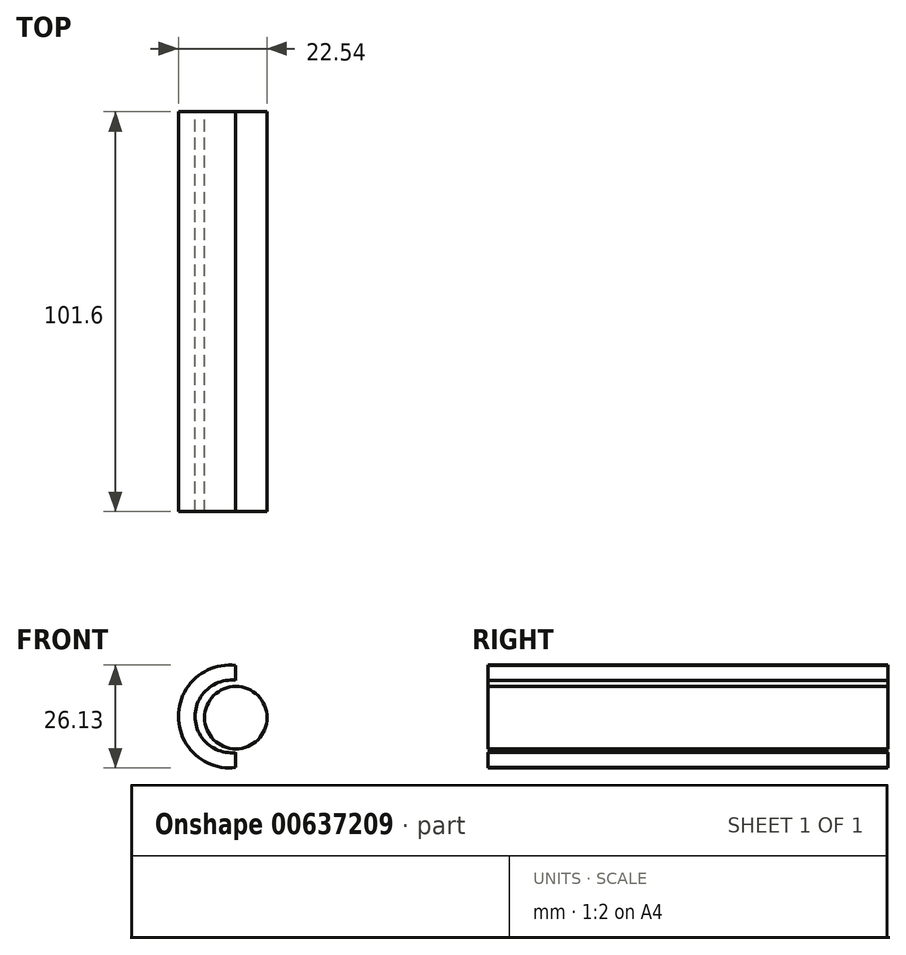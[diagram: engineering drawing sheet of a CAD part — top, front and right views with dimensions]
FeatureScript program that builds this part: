
annotation { "Feature Type Name" : "Feature", "Feature Type Description" : "" }
export const myFeature = defineFeature(function(context is Context, id is Id, definition is map)
    precondition{}
    {
        {
            var Q0;
            Q0=qCreatedBy(makeId("Front.planeOp"),FACE);
            var sketch = newSketch(context, id + "F0", { "sketchPlane" : qUnion([Q0])});
            skArc(sketch, "E0", {"start": v(0, 9.45) * mm, "mid": v(-10.35, 0.29) * mm, "end": v(0, -8.88) * mm});
            skLineSegment(sketch, "E1", {"start": v(0, 9.45) * mm, "end": v(0, 13.26) * mm});
            skLineSegment(sketch, "E2", {"start": v(0, -8.88) * mm, "end": v(0, -12.69) * mm});
            skArc(sketch, "E3", {"start": v(0, 13.26) * mm, "mid": v(-14.6, 0.29) * mm, "end": v(0, -12.69) * mm});
            skCircle(sketch, "E4", {"center": v(0, 0) * mm, "radius": 7.94 * mm});
            skSolve(sketch);
        }
        {
            var Q0;
            Q0 = qSketchRegion(id + "F0", true);
            extrude(context, id + "F1", {"entities" : qUnion([Q0]), "depth" : 101.6 * mm, "offsetDistance" : 25.4 * mm});
        }
    });
